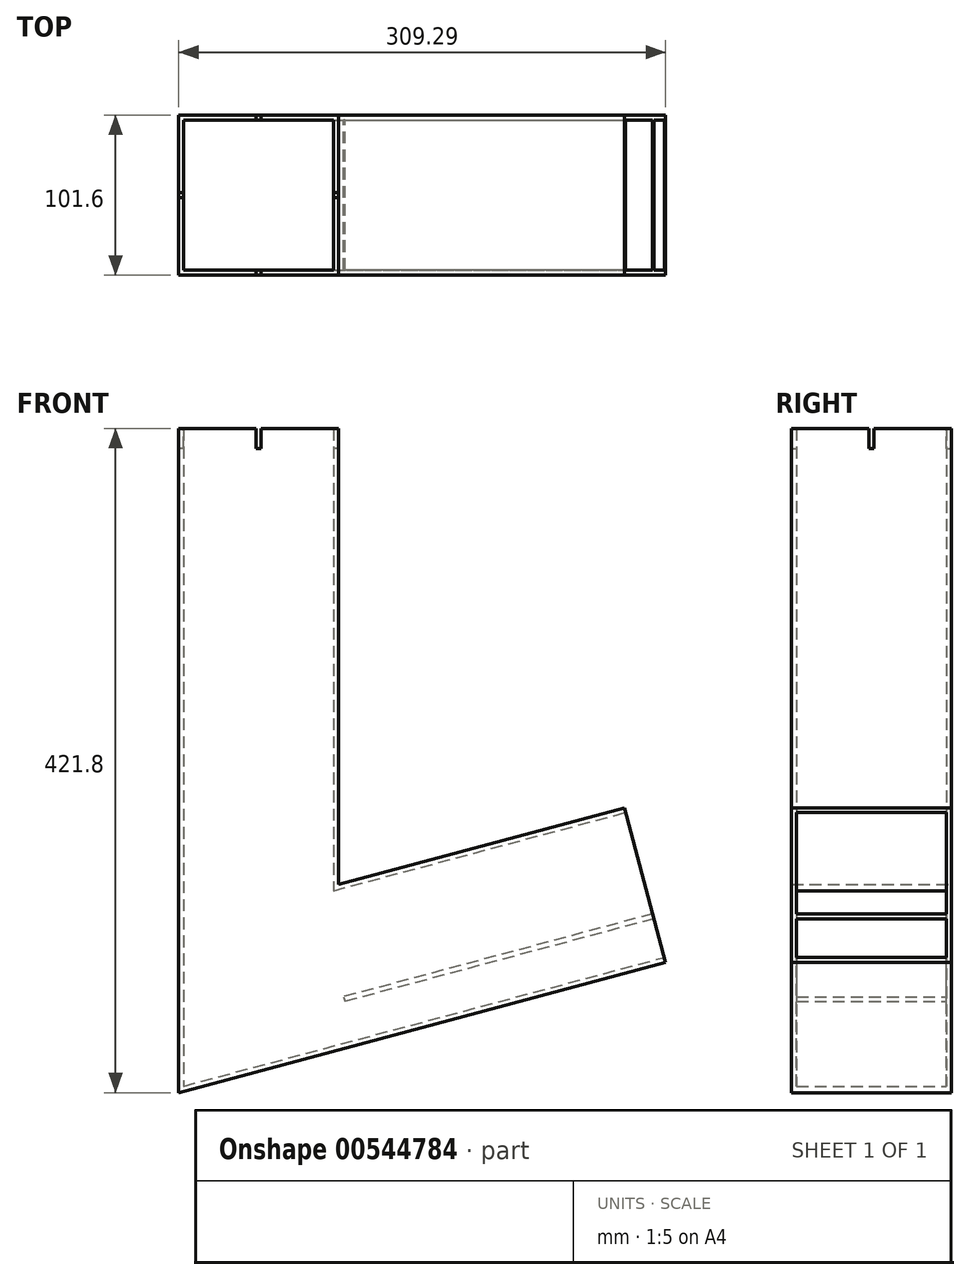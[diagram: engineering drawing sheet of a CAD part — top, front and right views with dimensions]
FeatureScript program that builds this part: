
annotation { "Feature Type Name" : "Feature", "Feature Type Description" : "" }
export const myFeature = defineFeature(function(context is Context, id is Id, definition is map)
    precondition{}
    {
        {
            var Q0;
            Q0=qCreatedBy(makeId("Top.planeOp"),FACE);
            var sketch = newSketch(context, id + "F0", { "sketchPlane" : qUnion([Q0])});
            skLineSegment(sketch, "E0.bottom", {"start": v(-50.8, 50.8) * mm, "end": v(50.8, 50.8) * mm});
            skLineSegment(sketch, "E0.top", {"start": v(-50.8, -50.8) * mm, "end": v(50.8, -50.8) * mm});
            skLineSegment(sketch, "E0.left", {"start": v(-50.8, 50.8) * mm, "end": v(-50.8, -50.8) * mm});
            skLineSegment(sketch, "E0.right", {"start": v(50.8, 50.8) * mm, "end": v(50.8, -50.8) * mm});
            skPoint(sketch, "E0.middle", {"position": v(0, 0) * mm});
            skLineSegment(sketch, "E1.bottom", {"start": v(-47.62, 47.62) * mm, "end": v(47.63, 47.62) * mm});
            skLineSegment(sketch, "E1.top", {"start": v(-47.63, -47.63) * mm, "end": v(47.62, -47.63) * mm});
            skLineSegment(sketch, "E1.left", {"start": v(-47.62, 47.62) * mm, "end": v(-47.63, -47.63) * mm});
            skLineSegment(sketch, "E1.right", {"start": v(47.63, 47.63) * mm, "end": v(47.62, -47.62) * mm});
            skSolve(sketch);
        }
        {
            var Q0;
            Q0=qCreatedBy(makeId("Front.planeOp"),FACE);
            var sketch = newSketch(context, id + "F1", { "sketchPlane" : qUnion([Q0])});
            skLineSegment(sketch, "E2", {"start": v(0, 0) * mm, "end": v(0, -355.6) * mm});
            skLineSegment(sketch, "E3", {"start": v(0, -355.6) * mm, "end": v(245.35, -289.86) * mm});
            skSolve(sketch);
        }
        {
            var Q0;
            Q0=makeQuery(id+"F0.imprint","IMPRINT",FACE,{"disambiguationData":[TD([[makeQuery(id+"F0.imprint","IMPRINT",EDGE,{"derivedFrom":sQuery(id+"F0.wireOp",EDGE,"E0.bottom")}),-1.0]])]});
            var Q1;
            Q1=sQuery(id+"F1.wireOp",EDGE,"E2");
            var Q2;
            Q2=sQuery(id+"F1.wireOp",EDGE,"E3");
            sweep(context, id + "F2", {"profiles" : qUnion([Q0]), "path" : qUnion([Q1, Q2])});
        }
        {
            var Q0;
            Q0=makeQuery(id+"F2.opSweep","CAP_FACE",FACE,{"disambiguationData":[OSD([sQuery(id+"F0.wireOp",EDGE,"E0.bottom"),sQuery(id+"F0.wireOp",EDGE,"E0.top"),sQuery(id+"F0.wireOp",EDGE,"E0.left"),sQuery(id+"F0.wireOp",EDGE,"E0.right"),sQuery(id+"F0.wireOp",EDGE,"E1.bottom"),sQuery(id+"F0.wireOp",EDGE,"E1.top"),sQuery(id+"F0.wireOp",EDGE,"E1.left"),sQuery(id+"F0.wireOp",EDGE,"E1.right"),sQuery(id+"F1.wireOp",VERTEX,"E3.end")])],"isStart":false});
            var sketch = newSketch(context, id + "F3", { "sketchPlane" : qUnion([Q0])});
            skLineSegment(sketch, "E4.bottom", {"start": v(-50.8, -362.53) * mm, "end": v(50.8, -362.53) * mm});
            skLineSegment(sketch, "E4.top", {"start": v(-50.8, -365.7) * mm, "end": v(50.8, -365.7) * mm});
            skLineSegment(sketch, "E4.left", {"start": v(-50.8, -362.53) * mm, "end": v(-50.8, -365.7) * mm});
            skLineSegment(sketch, "E4.right", {"start": v(50.8, -362.53) * mm, "end": v(50.8, -365.7) * mm});
            skSolve(sketch);
        }
        {
            var Q0;
            {var subQ0=sQuery(id+"F3.wireOp",EDGE,"E4.bottom");var subQ1=sQuery(id+"F1.wireOp",VERTEX,"E3.end");var subQ2=makeQuery(id+"F2.opSweep","CAP_EDGE",EDGE,{"disambiguationData":[OSD([sQuery(id+"F0.wireOp",EDGE,"E1.top"),subQ1])],"isStart":false});var subQ3=makeQuery(id+"F3.imprint","INTERSECT",VERTEX,{"derivedFrom":[subQ2,subQ0]});Q0=makeQuery(id+"F3.imprint","IMPRINT",FACE,{"disambiguationData":[TD([[makeQuery(id+"F3.imprint","IMPRINT",EDGE,{"disambiguationData":[TD([[subQ3,-1.0]])],"derivedFrom":subQ0}),-1.0]])]});}
            var Q1;
            {var subQ0=sQuery(id+"F3.wireOp",EDGE,"E4.right");Q1=makeQuery(id+"F3.imprint","IMPRINT",FACE,{"disambiguationData":[TD([[makeQuery(id+"F3.imprint","IMPRINT",EDGE,{"derivedFrom":subQ0}),1.0]])]});}
            var Q2;
            {var subQ0=sQuery(id+"F3.wireOp",EDGE,"E4.left");Q2=makeQuery(id+"F3.imprint","IMPRINT",FACE,{"disambiguationData":[TD([[makeQuery(id+"F3.imprint","IMPRINT",EDGE,{"derivedFrom":subQ0}),1.0]])]});}
            extrude(context, id + "F4", {"entities" : qUnion([Q0, Q1, Q2]), "operationType" : NewBodyOperationType.ADD, "oppositeDirection" : true, "depth" : 203.2 * mm, "offsetDistance" : 25.4 * mm});
        }
        {
            var Q0;
            Q0=makeQuery(id+"F2.opSweep","SWEPT_FACE",FACE,{"disambiguationData":[OSD([sQuery(id+"F0.wireOp",EDGE,"E0.bottom"),sQuery(id+"F1.wireOp",EDGE,"E2")])]});
            var sketch = newSketch(context, id + "F5", { "sketchPlane" : qUnion([Q0])});
            skLineSegment(sketch, "E5.bottom", {"start": v(-1.59, 0) * mm, "end": v(1.59, 0) * mm});
            skLineSegment(sketch, "E5.top", {"start": v(-1.59, -12.7) * mm, "end": v(1.59, -12.7) * mm});
            skLineSegment(sketch, "E5.left", {"start": v(-1.59, 0) * mm, "end": v(-1.59, -12.7) * mm});
            skLineSegment(sketch, "E5.right", {"start": v(1.59, 0) * mm, "end": v(1.59, -12.7) * mm});
            skSolve(sketch);
        }
        {
            var Q0;
            Q0=makeQuery(id+"F5.imprint","IMPRINT",FACE,{"disambiguationData":[TD([[makeQuery(id+"F5.imprint","IMPRINT",EDGE,{"derivedFrom":sQuery(id+"F5.wireOp",EDGE,"E5.bottom")}),1.0]])]});
            extrude(context, id + "F6", {"entities" : qUnion([Q0]), "operationType" : NewBodyOperationType.REMOVE, "endBound" : BoundingType.THROUGH_ALL, "oppositeDirection" : true, "depth" : 25.4 * mm, "offsetDistance" : 25.4 * mm});
        }
        {
            var Q0;
            Q0=makeQuery(id+"F2.opSweep","SWEPT_FACE",FACE,{"disambiguationData":[OSD([sQuery(id+"F0.wireOp",EDGE,"E0.left"),sQuery(id+"F1.wireOp",EDGE,"E2")])]});
            var sketch = newSketch(context, id + "F7", { "sketchPlane" : qUnion([Q0])});
            skLineSegment(sketch, "E6.bottom", {"start": v(-1.59, 0) * mm, "end": v(1.59, 0) * mm});
            skLineSegment(sketch, "E6.top", {"start": v(-1.59, -12.7) * mm, "end": v(1.59, -12.7) * mm});
            skLineSegment(sketch, "E6.left", {"start": v(-1.59, 0) * mm, "end": v(-1.59, -12.7) * mm});
            skLineSegment(sketch, "E6.right", {"start": v(1.59, 0) * mm, "end": v(1.59, -12.7) * mm});
            skSolve(sketch);
        }
        {
            var Q0;
            Q0=makeQuery(id+"F7.imprint","IMPRINT",FACE,{"disambiguationData":[TD([[makeQuery(id+"F7.imprint","IMPRINT",EDGE,{"derivedFrom":sQuery(id+"F7.wireOp",EDGE,"E6.bottom")}),1.0]])]});
            extrude(context, id + "F8", {"entities" : qUnion([Q0]), "operationType" : NewBodyOperationType.REMOVE, "endBound" : BoundingType.THROUGH_ALL, "oppositeDirection" : true, "depth" : 25.4 * mm, "offsetDistance" : 25.4 * mm});
        }
    });
